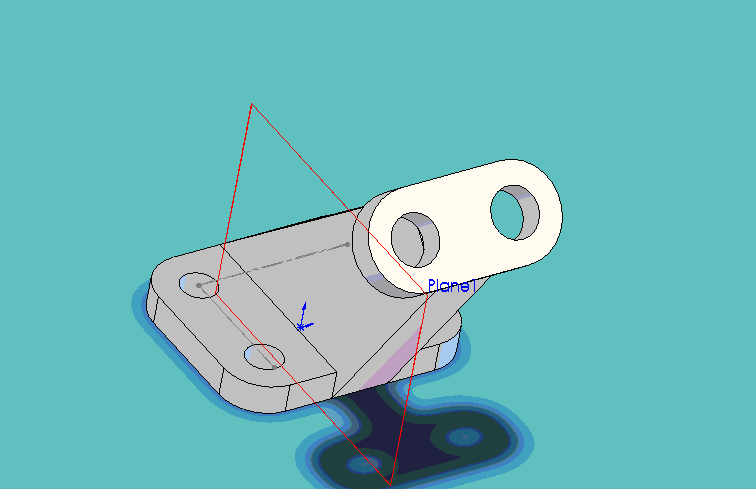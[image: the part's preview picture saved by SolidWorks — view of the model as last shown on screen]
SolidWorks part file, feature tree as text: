
SOLIDWORKS PART (.sldprt)
format: sldprt  version: not decoded by parser v0  size: 141,312 bytes
history: native  units: mm
features: sketch x6, plane x4, extrude x2, cut_extrude x2, material x1, pattern_linear x1, fillet x1 (+10 scaffold rows collapsed)
feature tree (27):
  scaffold x10  (default folders/planes/origin — collapsed)
  material  "Material <not specified>"
  plane  "Frontal"
  plane  "Horizontal"
  plane  "Profile"
  sketch  "Sketch1"  dims[D1=74.0mm D2=59.0mm]
  extrude  "Extrude1"  Depth=9mm
  sketch  "Sketch2"  dims[D3=10.5mm D1=13.0mm D2=13.0mm]
  cut_extrude  "Cut-Extrude1"  [1 undecoded]
  sketch  "Sketch3"
  pattern_linear  "LPattern1"  Count1=2 Count2=2 Spacing1=48mm Spacing2=33mm
  plane  "Plane1"  Offset=0.35mm
  sketch  "Sketch5"  dims[c1.D1=44.0deg c2.D1=84.36mm c2.D2=~57.323438mm c3.D2=45.0deg c4.D2=~12.829466mm c5.D2=119.0deg c6.D2=~90.380851mm c7.D2=44.0deg c7.D3=~45.750651mm c8.D3=61.0deg c8.D4=~32.434123mm c9.D4=~36.616342deg c10.D4=~32.434123mm c11.D4=45.0deg c12.D4=84.36mm c12.D1=~26.187481mm c13.D1=45.0deg c14.D1=18.0mm]
  sketch  "Sketch6"  dims[c1.D1=~20.069344mm c1.D2=14.5mm c2.D1=32.0mm c2.D3=16.0mm]
  extrude  "Extrude2"  Depth=9mm
  sketch  "Sketch7"  dims[D1=~6.516514mm]
  cut_extrude  "Cut-Extrude2"  Depth=9mm
  fillet  "Fillet8"  Radius=13mm
decode coverage: 10 of 12 modeling features carry decoded parameters
note: ~ marks probable driven/reference dimensions
note: 1 parameter value undecoded
note: suppression state not decoded; provenance and decode notes live in map.json
